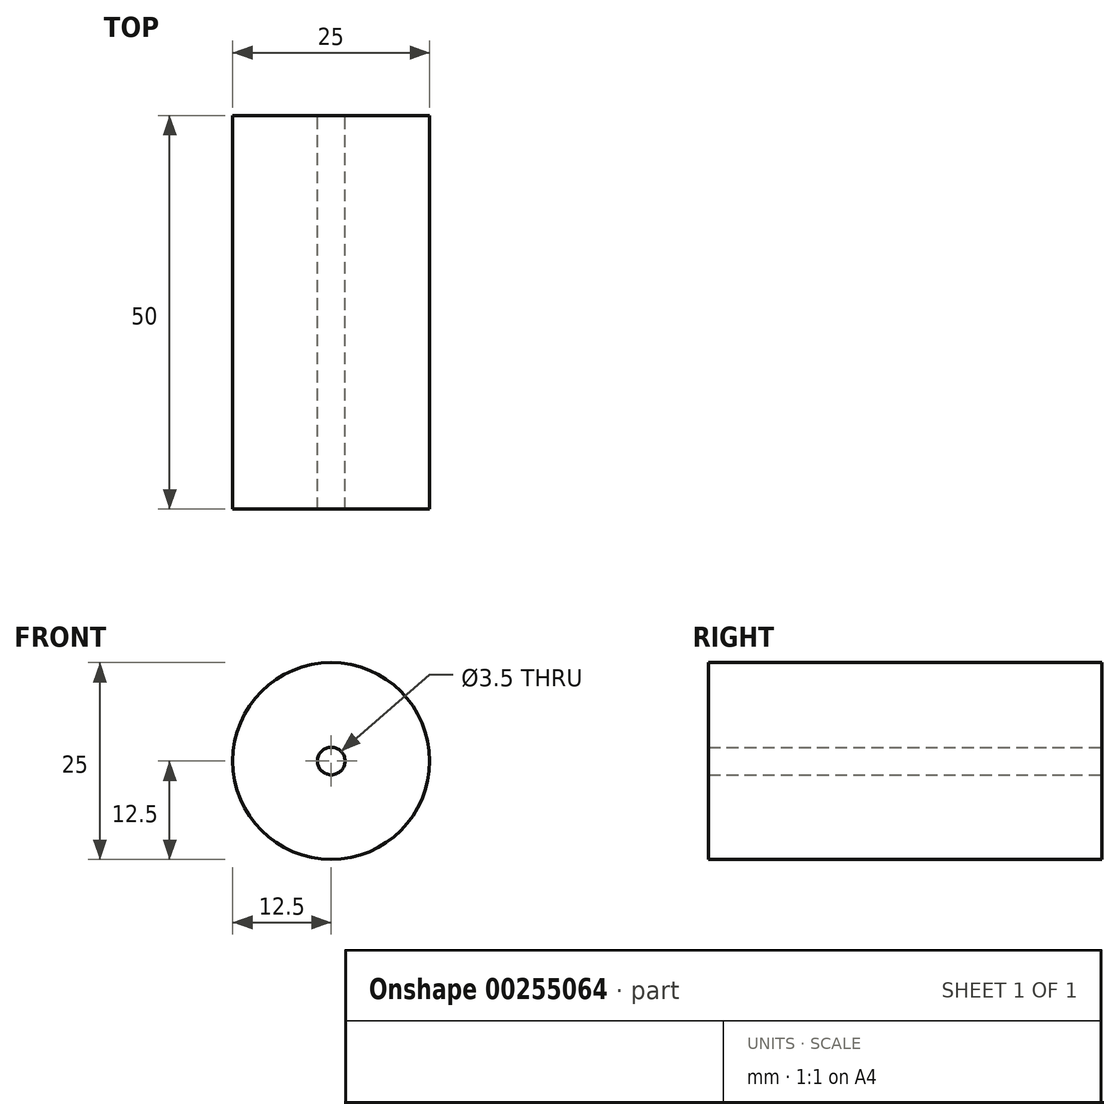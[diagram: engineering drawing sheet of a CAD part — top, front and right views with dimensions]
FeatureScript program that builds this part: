
annotation { "Feature Type Name" : "Feature", "Feature Type Description" : "" }
export const myFeature = defineFeature(function(context is Context, id is Id, definition is map)
    precondition{}
    {
        {
            var Q0;
            Q0=qCreatedBy(makeId("Front.planeOp"),FACE);
            var sketch = newSketch(context, id + "F0", { "sketchPlane" : qUnion([Q0])});
            skCircle(sketch, "E0", {"center": v(0, 0) * mm, "radius": 12.5 * mm});
            skCircle(sketch, "E1", {"center": v(0, 0) * mm, "radius": 1.75 * mm});
            skSolve(sketch);
        }
        {
            var Q0;
            Q0=makeQuery(id+"F0.imprint","IMPRINT",FACE,{"disambiguationData":[TD([[makeQuery(id+"F0.imprint","IMPRINT",EDGE,{"derivedFrom":sQuery(id+"F0.wireOp",EDGE,"E0")}),1.0]])]});
            extrude(context, id + "F1", {"entities" : qUnion([Q0]), "depth" : 50 * mm});
        }
    });
